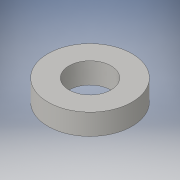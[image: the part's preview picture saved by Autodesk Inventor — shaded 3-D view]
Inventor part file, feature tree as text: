
AUTODESK INVENTOR PART (.ipt)
format: ipt  version: 2016 (Build 200138000, 138)  size: 107,008 bytes
history: native  units: in
note: dims shown in document units (in); Inventor stores cm internally (conversion verified against a paired STEP export)
features: extrude x1, sketch x1
ambient origin geometry x8: Origin, YZ Plane, XZ Plane, XY Plane, X Axis, Y Axis, Z Axis, Center Point
bodies: Solid1 (feature_tree)
feature tree (2):
  extrude  "Extrusion1"  Depth=0.25in
  sketch  "Sketch1"  dims[d0=0.5in d1=1.0in d2=0.25in d3=0.0in]
